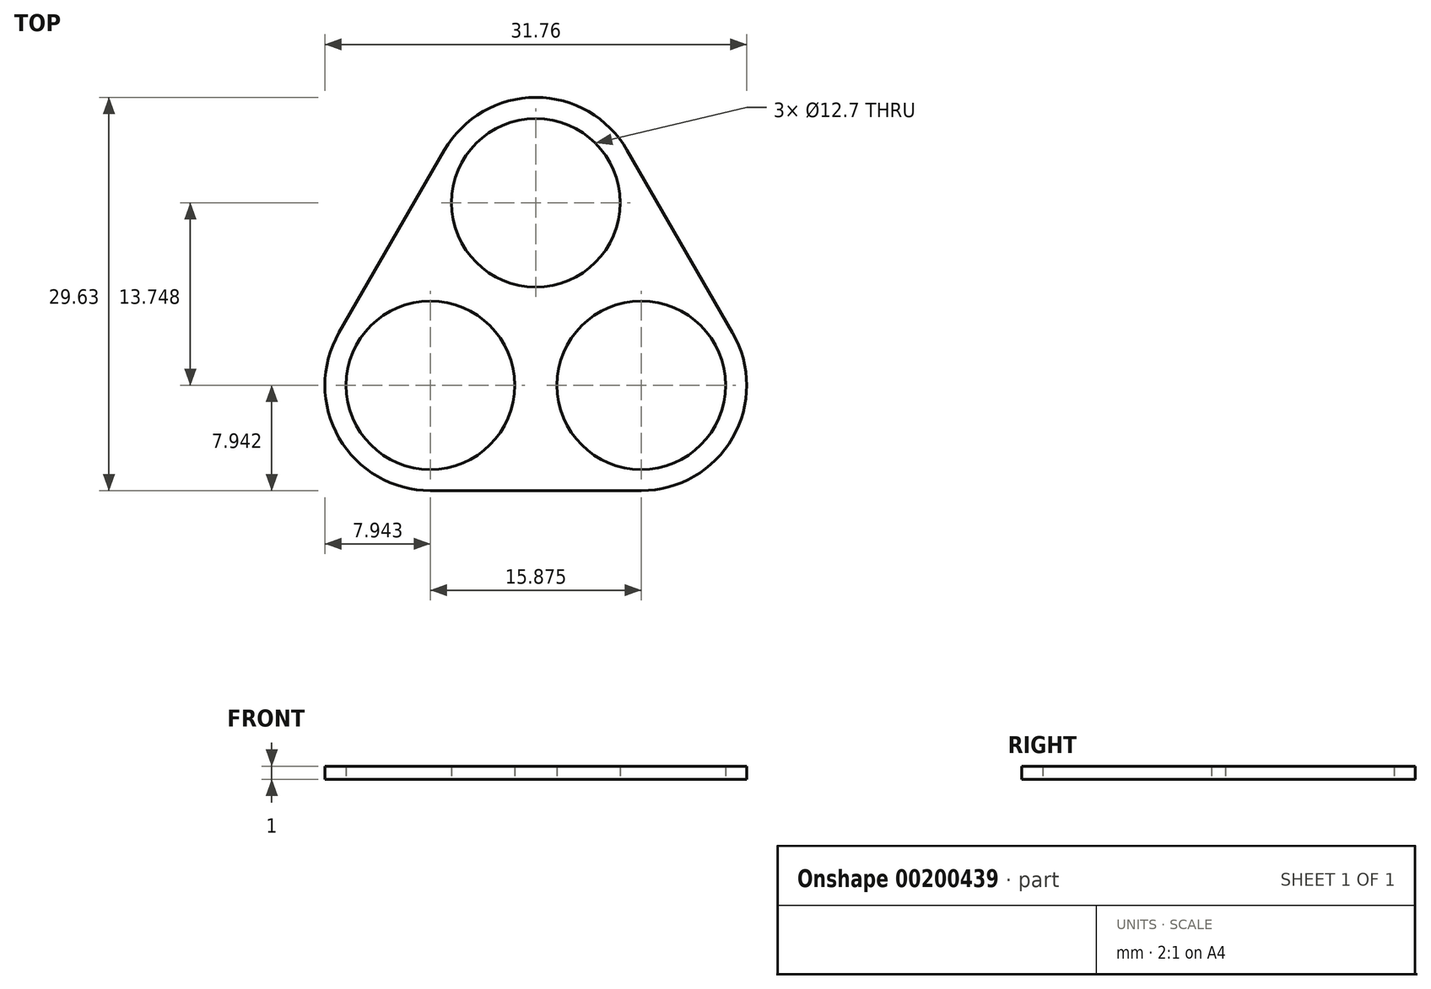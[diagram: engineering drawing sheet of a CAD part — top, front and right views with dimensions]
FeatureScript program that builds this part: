
annotation { "Feature Type Name" : "Feature", "Feature Type Description" : "" }
export const myFeature = defineFeature(function(context is Context, id is Id, definition is map)
    precondition{}
    {
        {
            var Q0;
            Q0=qCreatedBy(makeId("Top.planeOp"),FACE);
            var sketch = newSketch(context, id + "F0", { "sketchPlane" : qUnion([Q0])});
            skCircle(sketch, "E0", {"center": v(0, 0) * mm, "radius": 6.35 * mm});
            skCircle(sketch, "E1", {"center": v(0, 0) * mm, "radius": 7.94 * mm});
            skCircle(sketch, "E2", {"center": v(7.94, -13.75) * mm, "radius": 6.35 * mm});
            skCircle(sketch, "E3", {"center": v(7.94, -13.75) * mm, "radius": 7.94 * mm});
            skCircle(sketch, "E4", {"center": v(-7.94, -13.75) * mm, "radius": 6.35 * mm});
            skCircle(sketch, "E5", {"center": v(-7.94, -13.75) * mm, "radius": 7.94 * mm});
            skLineSegment(sketch, "E6", {"start": v(-14.81, -9.78) * mm, "end": v(-6.87, 3.97) * mm});
            skLineSegment(sketch, "E7", {"start": v(-7.94, -21.69) * mm, "end": v(7.94, -21.69) * mm});
            skLineSegment(sketch, "E8", {"start": v(14.81, -9.78) * mm, "end": v(6.87, 3.97) * mm});
            skSolve(sketch);
        }
        {
            var Q0;
            {var subQ0=sQuery(id+"F0.wireOp",EDGE,"E6");Q0=makeQuery(id+"F0.imprint","IMPRINT",FACE,{"disambiguationData":[TD([[makeQuery(id+"F0.imprint","IMPRINT",EDGE,{"derivedFrom":subQ0}),-1.0]])]});}
            var Q1;
            Q1=makeQuery(id+"F0.imprint","IMPRINT",FACE,{"disambiguationData":[TD([[makeQuery(id+"F0.imprint","IMPRINT",EDGE,{"derivedFrom":sQuery(id+"F0.wireOp",EDGE,"E4")}),-1.0]])]});
            var Q2;
            {var subQ0=sQuery(id+"F0.wireOp",EDGE,"E7");Q2=makeQuery(id+"F0.imprint","IMPRINT",FACE,{"disambiguationData":[TD([[makeQuery(id+"F0.imprint","IMPRINT",EDGE,{"derivedFrom":subQ0}),1.0]])]});}
            var Q3;
            Q3=makeQuery(id+"F0.imprint","IMPRINT",FACE,{"disambiguationData":[TD([[makeQuery(id+"F0.imprint","IMPRINT",EDGE,{"derivedFrom":sQuery(id+"F0.wireOp",EDGE,"E2")}),-1.0]])]});
            var Q4;
            {var subQ0=sQuery(id+"F0.wireOp",EDGE,"E8");Q4=makeQuery(id+"F0.imprint","IMPRINT",FACE,{"disambiguationData":[TD([[makeQuery(id+"F0.imprint","IMPRINT",EDGE,{"derivedFrom":subQ0}),1.0]])]});}
            var Q5;
            {var subQ0=sQuery(id+"F0.wireOp",EDGE,"E5");var subQ1=sQuery(id+"F0.wireOp",EDGE,"E1");var subQ2=makeQuery(id+"F0.imprint","INTERSECT",VERTEX,{"derivedFrom":[subQ1,subQ0]});Q5=makeQuery(id+"F0.imprint","IMPRINT",FACE,{"disambiguationData":[TD([[makeQuery(id+"F0.imprint","IMPRINT",EDGE,{"disambiguationData":[TD([[subQ2,-1.0]])],"derivedFrom":subQ1}),-1.0]])]});}
            var Q6;
            Q6=makeQuery(id+"F0.imprint","IMPRINT",FACE,{"disambiguationData":[TD([[makeQuery(id+"F0.imprint","IMPRINT",EDGE,{"derivedFrom":sQuery(id+"F0.wireOp",EDGE,"E0")}),-1.0]])]});
            extrude(context, id + "F1", {"entities" : qUnion([Q0, Q1, Q2, Q3, Q4, Q5, Q6]), "depth" : 1 * mm});
        }
    });
